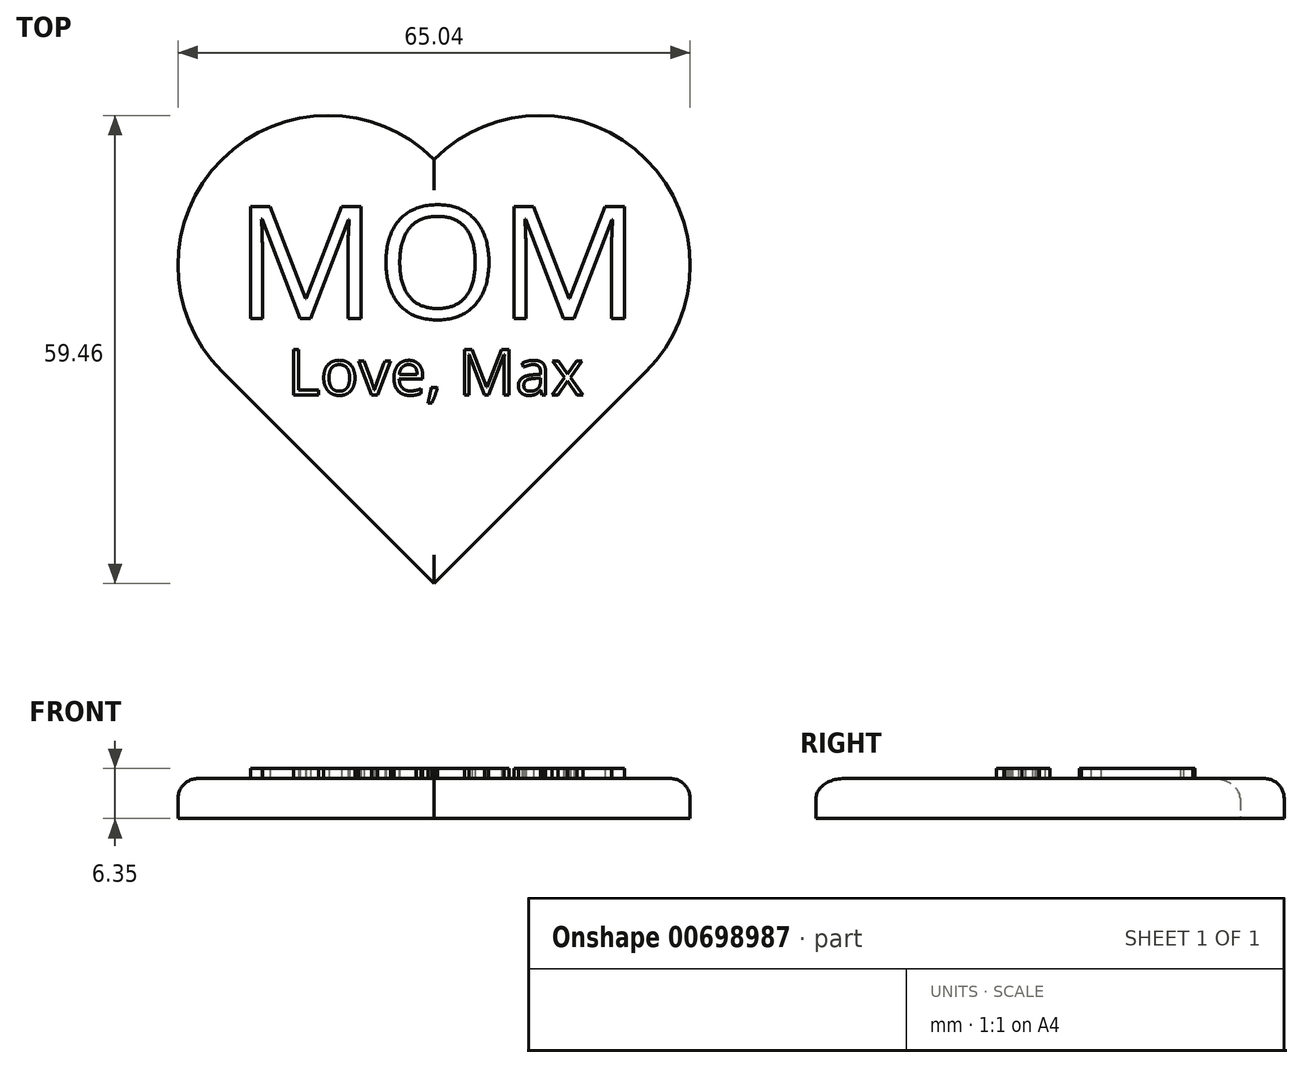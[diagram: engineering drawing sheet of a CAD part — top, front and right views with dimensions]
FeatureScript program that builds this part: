
annotation { "Feature Type Name" : "Feature", "Feature Type Description" : "" }
export const myFeature = defineFeature(function(context is Context, id is Id, definition is map)
    precondition{}
    {
        {
            var Q0;
            Q0=qCreatedBy(makeId("Top.planeOp"),FACE);
            var sketch = newSketch(context, id + "F0", { "sketchPlane" : qUnion([Q0])});
            skLineSegment(sketch, "E0", {"start": v(-40.54, 22.68) * mm, "end": v(-40.54, -15.42) * mm});
            skLineSegment(sketch, "E1", {"start": v(-40.54, -15.42) * mm, "end": v(-2.44, -15.42) * mm});
            skArc(sketch, "E2", {"start": v(-2.44, 22.68) * mm, "mid": v(-21.49, 41.73) * mm, "end": v(-40.54, 22.68) * mm});
            skArc(sketch, "E3", {"start": v(-2.44, -15.42) * mm, "mid": v(16.61, 3.63) * mm, "end": v(-2.44, 22.68) * mm});
            skPoint(sketch, "E4.endSnap0", {"position": v(-21.49, 41.73) * mm});
            skPoint(sketch, "E5.endSnap0", {"position": v(16.61, 3.63) * mm});
            skSolve(sketch);
        }
        {
            var Q0;
            Q0=makeQuery(id+"F0.imprint","IMPRINT",FACE,{"disambiguationData":[TD([[makeQuery(id+"F0.imprint","IMPRINT",EDGE,{"derivedFrom":sQuery(id+"F0.wireOp",EDGE,"E0")}),1.0]])]});
            extrude(context, id + "F1", {"entities" : qUnion([Q0]), "depth" : 5.08 * mm, "offsetDistance" : 25.4 * mm});
        }
        {
            var Q0;
            Q0=makeQuery(id+"F1.opExtrude","SWEPT_BODY",BODY,{"disambiguationData":[OSD([sQuery(id+"F0.wireOp",EDGE,"E0"),sQuery(id+"F0.wireOp",EDGE,"E1"),sQuery(id+"F0.wireOp",EDGE,"E2"),sQuery(id+"F0.wireOp",EDGE,"E3")])]});
            var Q1;
            Q1=makeQuery(id+"F1.opExtrude","SWEPT_EDGE",EDGE,{"disambiguationData":[OSD([sQuery(id+"F0.wireOp",EDGE,"E0"),sQuery(id+"F0.wireOp",EDGE,"E1")])]});
            transform(context, id + "F2", {"entities" : qUnion([Q0]), "transformType" : TransformType.ROTATION, "transformAxis" : qUnion([Q1]), "angle" : 315 * degree, "makeCopy" : false});
        }
        {
            var Q0;
            Q0=makeQuery(id+"F1.opExtrude","CAP_FACE",FACE,{"disambiguationData":[OSD([sQuery(id+"F0.wireOp",EDGE,"E0"),sQuery(id+"F0.wireOp",EDGE,"E1"),sQuery(id+"F0.wireOp",EDGE,"E2"),sQuery(id+"F0.wireOp",EDGE,"E3")])],"isStart":false});
            var sketch = newSketch(context, id + "F3", { "sketchPlane" : qUnion([Q0])});
            skText(sketch, "E6", { "text": "MOM", "fontName": "OpenSans-Regular.ttf"});
            skText(sketch, "E7", { "text": "Love, Max", "fontName": "OpenSans-Regular.ttf"});
            const initialGuessF3  = {"E6": [-0.06583, 0.01826, 1, 0, 0.01433], "E7": [-0.0592, 0.00854, 1, 0, 0.00581]};
            skSetInitialGuess(sketch, initialGuessF3);
            skSolve(sketch);
        }
        {
            var Q0;
            Q0=qSketchRegion(id+"F3",true);
            extrude(context, id + "F4", {"entities" : qUnion([Q0]), "operationType" : NewBodyOperationType.ADD, "depth" : 1.27 * mm, "offsetDistance" : 25.4 * mm});
        }
        {
            var Q0;
            Q0=makeQuery(id+"F1.opExtrude","CAP_EDGE",EDGE,{"disambiguationData":[OSD([sQuery(id+"F0.wireOp",EDGE,"E3")])],"isStart":false});
            var Q1;
            Q1=makeQuery(id+"F1.opExtrude","CAP_EDGE",EDGE,{"disambiguationData":[OSD([sQuery(id+"F0.wireOp",EDGE,"E2")])],"isStart":false});
            fillet(context, id + "F5", {"entities" : qUnion([Q0, Q1]), "radius" : 2.54 * mm, "tangentPropagation" : true, "allowEdgeOverflow" : false});
        }
    });
